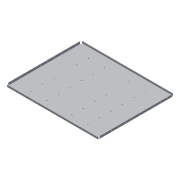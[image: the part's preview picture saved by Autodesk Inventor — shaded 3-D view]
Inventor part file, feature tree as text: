
AUTODESK INVENTOR PART (.ipt)
format: ipt  version: 2016 SP2 (Build 200236200, 236)  size: 225,280 bytes
history: native  units: in
note: dims shown in document units (in); Inventor stores cm internally (conversion verified against a paired STEP export)
features: reference x6, hole x1, sketch x1
ambient origin geometry x8: Origin, YZ Plane, XZ Plane, XY Plane, X Axis, Y Axis, Z Axis, Center Point
bodies: Solid1 (feature_tree)
feature tree (8):
  hole  "Hole2"  [1 undecoded]
  sketch  "Sketch2"  dims[d10=0.1693in d11=0.2362in d12=0.1575in d13=0.0787in d14=90.0deg d15=0.315in d16=0.8108in]
  reference  "Reference2"
  reference  "Reference3"
  reference  "Reference4"
  reference  "Reference5"
  reference  "Reference6"
  reference  "Reference7"
note: 1 required parameter value undecoded (feature->parameter linkage not recoverable at this tier; creation-order binding heuristic only, values carry confidence <= 0.55)
